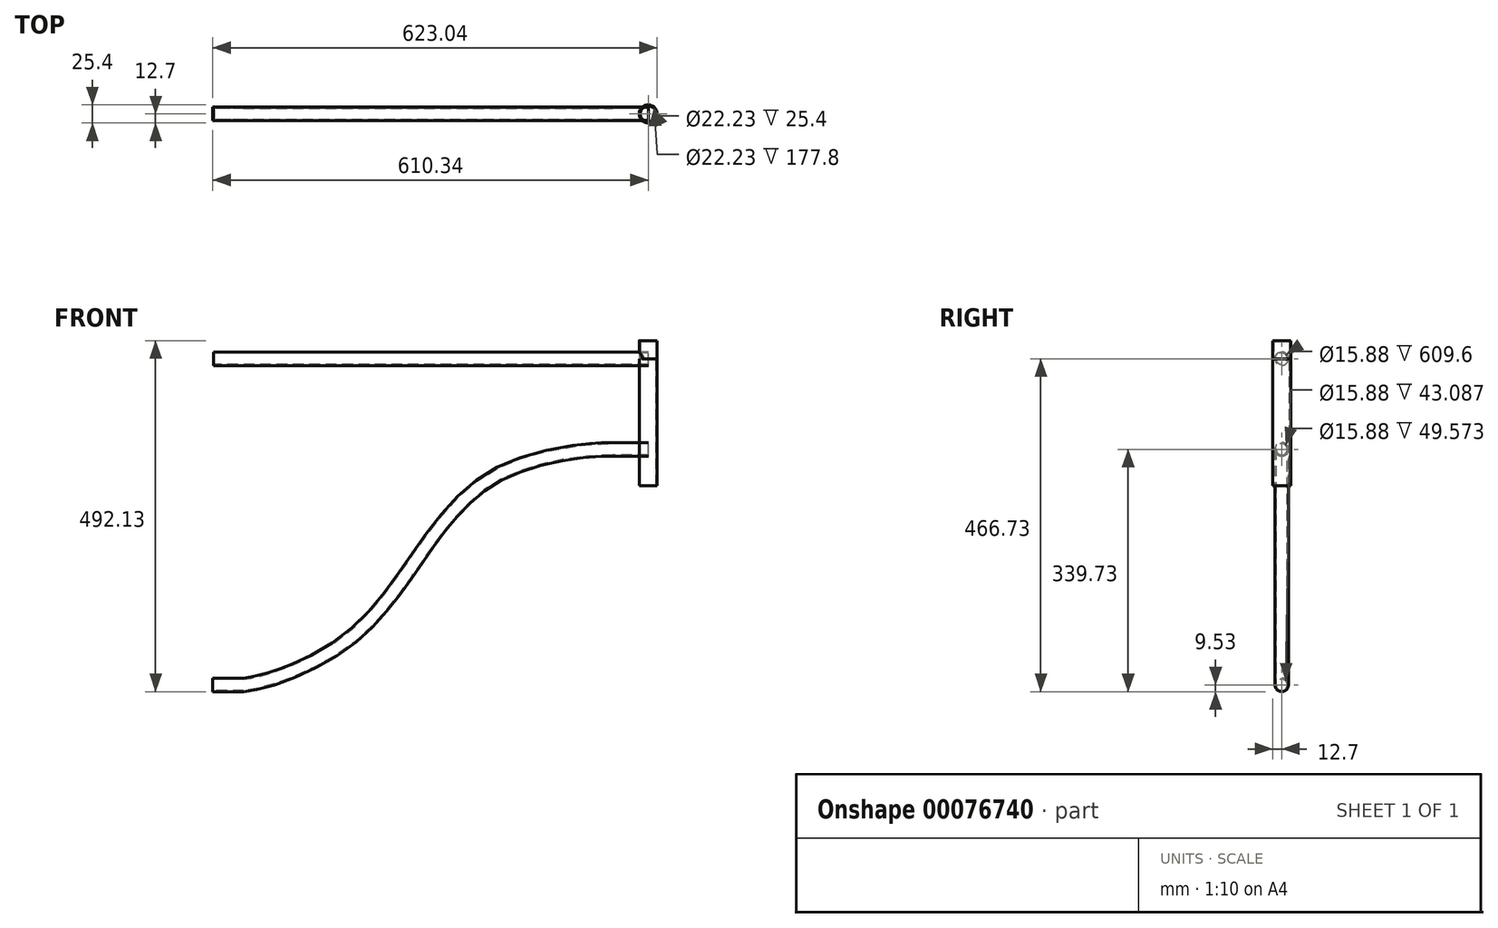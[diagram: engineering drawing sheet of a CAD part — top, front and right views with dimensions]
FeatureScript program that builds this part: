
annotation { "Feature Type Name" : "Feature", "Feature Type Description" : "" }
export const myFeature = defineFeature(function(context is Context, id is Id, definition is map)
    precondition{}
    {
        {
            var Q0;
            Q0=qCreatedBy(makeId("Top.planeOp"),FACE);
            var sketch = newSketch(context, id + "F0", { "sketchPlane" : qUnion([Q0])});
            skLineSegment(sketch, "E0", {"start": v(0, 0) * mm, "end": v(-609.6, 0) * mm});
            skCircle(sketch, "E1", {"center": v(0, 0) * mm, "radius": 12.7 * mm});
            skCircle(sketch, "E2", {"center": v(0, 0) * mm, "radius": 11.11 * mm});
            skSolve(sketch);
        }
        {
            var Q0;
            Q0=qCreatedBy(makeId("Front.planeOp"),FACE);
            var sketch = newSketch(context, id + "F1", { "sketchPlane" : qUnion([Q0])});
            skLineSegment(sketch, "E3", {"start": v(0, -127) * mm, "end": v(-49.57, -127) * mm});
            skLineSegment(sketch, "E4", {"start": v(-567.26, -457.2) * mm, "end": v(-610.34, -457.2) * mm});
            skFitSpline(sketch, "E5", {"points": [v(-49.57, -127) * mm, v(-220.16, -167.79) * mm, v(-413.68, -388.54) * mm, v(-567.26, -457.2) * mm], "startDerivative": vector(-181.41, 0) * mm, "endDerivative": vector(-173.67, 0) * mm});
            skLineSegment(sketch, "E6", {"start": v(-610.34, -457.2) * mm, "end": v(-610.34, 0) * mm});
            skSolve(sketch);
        }
        {
            var Q0;
            Q0=qCreatedBy(makeId("Right.planeOp"),FACE);
            var sketch = newSketch(context, id + "F2", { "sketchPlane" : qUnion([Q0])});
            skCircle(sketch, "E7", {"center": v(0, -127) * mm, "radius": 9.53 * mm});
            skCircle(sketch, "E8", {"center": v(0, 0) * mm, "radius": 9.53 * mm});
            skCircle(sketch, "E9", {"center": v(0, 0) * mm, "radius": 7.94 * mm});
            skCircle(sketch, "E10", {"center": v(0, -127) * mm, "radius": 7.94 * mm});
            skSolve(sketch);
        }
        {
            var Q0;
            Q0=makeQuery(id+"F2.imprint","IMPRINT",FACE,{"disambiguationData":[TD([[makeQuery(id+"F2.imprint","IMPRINT",EDGE,{"derivedFrom":sQuery(id+"F2.wireOp",EDGE,"E8")}),1.0]])]});
            var Q1;
            Q1=sQuery(id+"F0.wireOp",EDGE,"E0");
            sweep(context, id + "F3", {"profiles" : qUnion([Q0]), "path" : qUnion([Q1])});
        }
        {
            var Q0;
            Q0=makeQuery(id+"F2.imprint","IMPRINT",FACE,{"disambiguationData":[TD([[makeQuery(id+"F2.imprint","IMPRINT",EDGE,{"derivedFrom":sQuery(id+"F2.wireOp",EDGE,"E7")}),1.0]])]});
            var Q1;
            Q1=sQuery(id+"F1.wireOp",EDGE,"E3");
            var Q2;
            Q2=sQuery(id+"F1.wireOp",EDGE,"E5");
            var Q3;
            Q3=sQuery(id+"F1.wireOp",EDGE,"E4");
            sweep(context, id + "F4", {"profiles" : qUnion([Q0]), "path" : qUnion([Q1, Q2, Q3])});
        }
        {
            var Q0;
            Q0=makeQuery(id+"F0.imprint","IMPRINT",FACE,{"disambiguationData":[TD([[makeQuery(id+"F0.imprint","IMPRINT",EDGE,{"derivedFrom":sQuery(id+"F0.wireOp",EDGE,"E1")}),1.0]])]});
            extrude(context, id + "F5", {"entities" : qUnion([Q0]), "operationType" : NewBodyOperationType.ADD, "depth" : 25.4 * mm});
        }
        {
            var Q0;
            Q0=makeQuery(id+"F0.imprint","IMPRINT",FACE,{"disambiguationData":[TD([[makeQuery(id+"F0.imprint","IMPRINT",EDGE,{"derivedFrom":sQuery(id+"F0.wireOp",EDGE,"E1")}),1.0]])]});
            extrude(context, id + "F6", {"entities" : qUnion([Q0]), "oppositeDirection" : true, "depth" : 177.8 * mm});
        }
    });
